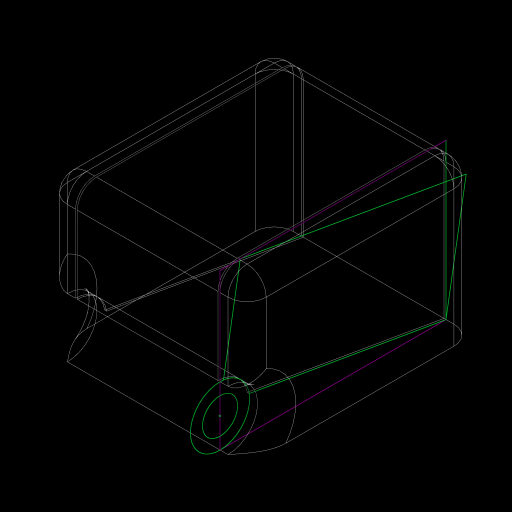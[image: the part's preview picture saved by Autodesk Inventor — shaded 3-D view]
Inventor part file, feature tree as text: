
AUTODESK INVENTOR PART (.ipt)
format: ipt  version: 2024 (Build 280153000, 153)  size: 280,064 bytes
history: native  units: in
note: dims shown in document units (in); Inventor stores cm internally (conversion verified against a paired STEP export)
features: sketch x6, extrude x6, projected_geometry x2, other x1, plane x1, mirror x1, fillet x1
ambient origin geometry x8: Origin, YZ Plane, XZ Plane, XY Plane, X Axis, Y Axis, Z Axis, Center Point
bodies: Solid1 (feature_tree)
feature tree (18):
  sketch  "Sketch1"  dims[d0=0.387in d1=0.763in d2=0.0in]
  extrude  "CAP"  Depth=0.763in TaperAngle=0.0deg
  sketch  "Sketch2"  dims[d7=0.92in d12=0.92in]
  other  "SHEATHING"
  extrude  "WIRE APROX"  Depth=0.92in
  plane  "Work Plane1"
  extrude  "RAXOR1 EXT"  Depth=0.0785in
  sketch  "Sketch11"  dims[d20=0.02in d21=3.0in d22=0.0in]
  sketch  "Sketch12"  dims[d25=0.129in d26=1.5in d29=0.77in d30=0.012in d31=0.0in d32=0.5504in d35=0.46in d46=1.3in d47=0.0in d48=1.3in d49=0.0in d54=0.012in d55=0.0in d82=0.6865in d83=90.0deg d84=0.6184in d85=1.0165in d86=0.77in d87=1.5in d88=1.4776in d89=0.6308in d90=0.823in d95=0.125in d23=0.5in d24=0.0344in d33=0.0344in d36=0.0344in d37=0.5in d38=0.0344in d50=0.5in d51=0.0344in d52=0.5in d53=0.0344in d56=0.5in d57=0.0344in d58=0.5in d59=0.0344in d63=0.5in d64=0.0344in d65=0.5in d66=0.0344in d67=0.0344in d74=0.5in d75=0.0344in d76=0.5in d77=0.0344in d96=0.0in d97=0.0in d98=0.0in]
  extrude  "WORKPIECE"  TaperAngle=360.0deg  [1 undecoded]
  extrude  "CAP CUTOUT"  Depth=3.0in TaperAngle=0.0deg
  extrude  "RAZ CUTOUT1"  Depth=0.125in
  mirror  "Mirror1"
  fillet  "Fillet8"  Radius=0.77in
  sketch  "Sketch3"  dims[d15=0.0785in d16=0.0785in]
  sketch  "Sketch5"  dims[d18=0.3815in d19=360.0deg]
  projected_geometry  "Projected Loop6"
  projected_geometry  "Projected Loop7"
note: 1 required parameter value undecoded (feature->parameter linkage not recoverable at this tier; creation-order binding heuristic only, values carry confidence <= 0.55)
